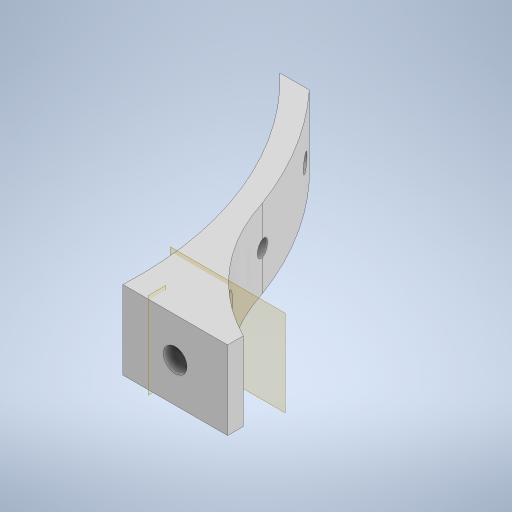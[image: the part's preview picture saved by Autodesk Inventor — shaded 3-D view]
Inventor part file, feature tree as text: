
AUTODESK INVENTOR PART (.ipt)
format: ipt  version: 2024.2 (Build 282272000, 272)  size: 298,496 bytes
history: native  units: mm
features: extrude x5, sketch x5, plane x2
ambient origin geometry x8: Origin, YZ Plane, XZ Plane, XY Plane, X Axis, Y Axis, Z Axis, Center Point
bodies: Solid1 (feature_tree)
feature tree (12):
  extrude  "Extrusion1"  Depth=50.0mm
  extrude  "Extrusion2"  Depth=20.0mm
  plane  "Work Plane1"
  extrude  "Extrusion3"  Depth=40.0mm
  plane  "Work Plane2"
  extrude  "Extrusion4"  Depth=15.0mm TaperAngle=0.0deg
  extrude  "Extrusion5"  Depth=10.0mm
  sketch  "Sketch1"  dims[d0=40.0mm d1=50.0mm]
  sketch  "Sketch2"  dims[d2=65.0mm d3=20.0mm]
  sketch  "Sketch3"  dims[d4=4.0mm d5=40.0mm]
  sketch  "Sketch4"  dims[d6=3.0mm d7=15.0mm d8=0.0mm]
  sketch  "Sketch6"  dims[d9=4.5mm d10=10.0mm d11=0.0mm d12=0.0mm d13=-10.0mm d14=9.0mm d15=6.0mm d16=10.0mm d17=0.0mm d18=0.0mm d19=-15.0mm d20=3.0mm d21=3.0mm d22=5.0mm d23=6.0mm d24=0.0mm d25=3.5mm d26=5.0mm d27=0.0mm d28=0.0mm]
